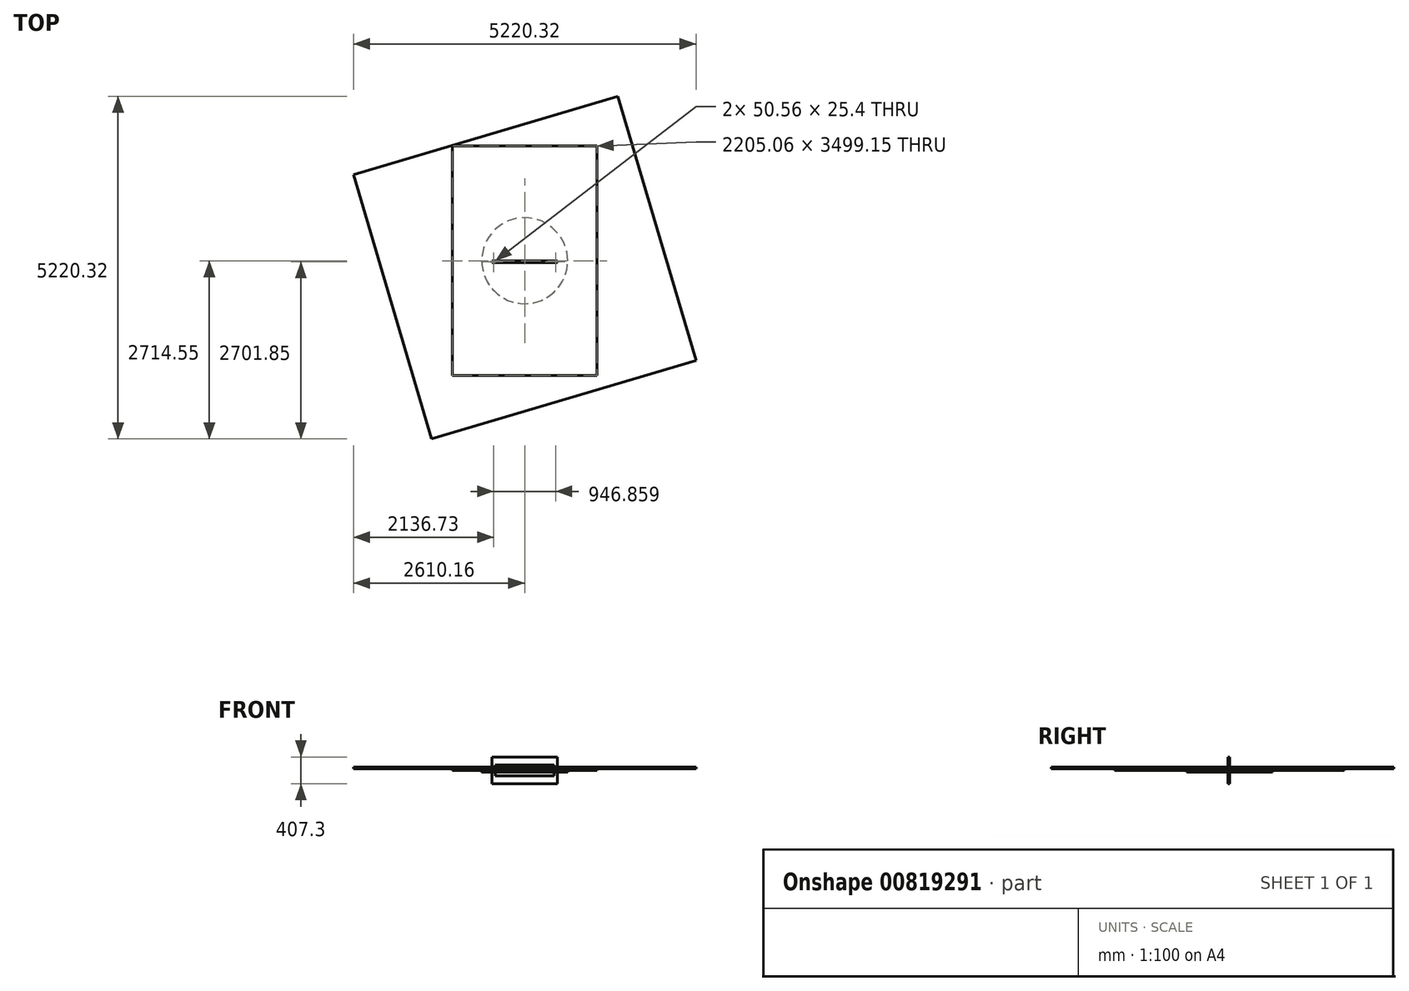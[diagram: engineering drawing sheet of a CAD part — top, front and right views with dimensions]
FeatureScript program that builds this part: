
annotation { "Feature Type Name" : "Feature", "Feature Type Description" : "" }
export const myFeature = defineFeature(function(context is Context, id is Id, definition is map)
    precondition{}
    {
        {
            var Q0;
            Q0=qCreatedBy(makeId("Front.planeOp"),FACE);
            var sketch = newSketch(context, id + "F0", { "sketchPlane" : qUnion([Q0])});
            skLineSegment(sketch, "E0.bottom", {"start": v(448.15, -82.7) * mm, "end": v(-448.15, -82.7) * mm});
            skLineSegment(sketch, "E0.top", {"start": v(448.15, 82.7) * mm, "end": v(-448.15, 82.7) * mm});
            skLineSegment(sketch, "E0.left", {"start": v(448.15, -82.7) * mm, "end": v(448.15, 82.7) * mm});
            skLineSegment(sketch, "E0.right", {"start": v(-448.15, -82.7) * mm, "end": v(-448.15, 82.7) * mm});
            skPoint(sketch, "E0.middle", {"position": v(0, 0) * mm});
            skLineSegment(sketch, "E1.bottom", {"start": v(-498.7, 203.65) * mm, "end": v(498.7, 203.65) * mm});
            skLineSegment(sketch, "E1.top", {"start": v(-498.7, -203.65) * mm, "end": v(498.7, -203.65) * mm});
            skLineSegment(sketch, "E1.left", {"start": v(-498.7, 203.65) * mm, "end": v(-498.7, -203.65) * mm});
            skLineSegment(sketch, "E1.right", {"start": v(498.7, 203.65) * mm, "end": v(498.7, -203.65) * mm});
            skSolve(sketch);
        }
        {
            var Q0;
            Q0=makeQuery(id+"F0.imprint","IMPRINT",FACE,{"disambiguationData":[TD([[makeQuery(id+"F0.imprint","IMPRINT",EDGE,{"derivedFrom":sQuery(id+"F0.wireOp",EDGE,"E0.bottom")}),1.0]])]});
            extrude(context, id + "F1", {"entities" : qUnion([Q0]), "depth" : 25.4 * mm, "offsetDistance" : 25.4 * mm});
        }
        {
            var Q0;
            Q0=qCreatedBy(makeId("Top.planeOp"),FACE);
            var sketch = newSketch(context, id + "F2", { "sketchPlane" : qUnion([Q0])});
            skLineSegment(sketch, "E2.bottom", {"start": v(-1102.53, -1749.57) * mm, "end": v(1102.53, -1749.57) * mm});
            skLineSegment(sketch, "E2.top", {"start": v(-1102.53, 1749.57) * mm, "end": v(1102.53, 1749.57) * mm});
            skLineSegment(sketch, "E2.left", {"start": v(-1102.53, -1749.57) * mm, "end": v(-1102.53, 1749.57) * mm});
            skLineSegment(sketch, "E2.right", {"start": v(1102.53, -1749.57) * mm, "end": v(1102.53, 1749.57) * mm});
            skPoint(sketch, "E2.middle", {"position": v(0, 0) * mm});
            skSolve(sketch);
        }
        {
            var Q0;
            Q0=makeQuery(id+"F2.imprint","IMPRINT",FACE,{"disambiguationData":[TD([[makeQuery(id+"F2.imprint","IMPRINT",EDGE,{"derivedFrom":sQuery(id+"F2.wireOp",EDGE,"E2.bottom")}),1.0]])]});
            extrude(context, id + "F3", {"entities" : qUnion([Q0]), "operationType" : NewBodyOperationType.ADD, "depth" : 25.4 * mm, "offsetDistance" : 25.4 * mm});
        }
        {
            var Q0;
            Q0=makeQuery(id+"F3.opExtrude","CAP_FACE",FACE,{"disambiguationData":[OSD([sQuery(id+"F2.wireOp",EDGE,"E2.bottom"),sQuery(id+"F2.wireOp",EDGE,"E2.top"),sQuery(id+"F2.wireOp",EDGE,"E2.left"),sQuery(id+"F2.wireOp",EDGE,"E2.right")])],"isStart":true});
            var sketch = newSketch(context, id + "F4", { "sketchPlane" : qUnion([Q0])});
            skCircle(sketch, "E3", {"center": v(0, 0) * mm, "radius": 654.69 * mm});
            skCircle(sketch, "E4", {"center": v(0, 0) * mm, "radius": 953.45 * mm});
            skCircle(sketch, "E5", {"center": v(0, 0) * mm, "radius": 1245.2 * mm});
            skSolve(sketch);
        }
        {
            var Q0;
            Q0=makeQuery(id+"F4.imprint","IMPRINT",FACE,{"disambiguationData":[TD([[makeQuery(id+"F4.imprint","IMPRINT",EDGE,{"derivedFrom":sQuery(id+"F4.wireOp",EDGE,"E3")}),1.0]])]});
            extrude(context, id + "F5", {"entities" : qUnion([Q0]), "operationType" : NewBodyOperationType.ADD, "depth" : 25.4 * mm, "offsetDistance" : 25.4 * mm});
        }
        {
            var Q0;
            Q0=makeQuery(id+"F3.opExtrude","CAP_FACE",FACE,{"disambiguationData":[OSD([sQuery(id+"F2.wireOp",EDGE,"E2.bottom"),sQuery(id+"F2.wireOp",EDGE,"E2.top"),sQuery(id+"F2.wireOp",EDGE,"E2.left"),sQuery(id+"F2.wireOp",EDGE,"E2.right")])],"isStart":false});
            var sketch = newSketch(context, id + "F6", { "sketchPlane" : qUnion([Q0])});
            skSolve(sketch);
        }
        {
            var Q0;
            {var subQ3=sQuery(id+"F2.wireOp",EDGE,"E2.bottom");Q0=makeQuery(id+"F6.imprint","IMPRINT",FACE,{"disambiguationData":[TD([[makeQuery(id+"F6.imprint","IMPRINT",EDGE,{"derivedFrom":makeQuery(id+"F3.opExtrude","CAP_EDGE",EDGE,{"disambiguationData":[OSD([subQ3])],"isStart":false})}),1.0]])]});}
            var sketch = newSketch(context, id + "F7", { "sketchPlane" : qUnion([Q0])});
            skCircle(sketch, "E6.cCircle", {"center": v(0, -104.4) * mm, "radius": 2100.34 * mm, "construction": true});
            skLineSegment(sketch, "E6.0", {"start": v(-2610.16, 1313.33) * mm, "end": v(1417.73, 2505.77) * mm});
            skLineSegment(sketch, "E6.1", {"start": v(1417.73, 2505.77) * mm, "end": v(2610.16, -1522.12) * mm});
            skLineSegment(sketch, "E6.2", {"start": v(2610.16, -1522.12) * mm, "end": v(-1417.73, -2714.55) * mm});
            skLineSegment(sketch, "E6.3", {"start": v(-1417.73, -2714.55) * mm, "end": v(-2610.16, 1313.33) * mm});
            skPoint(sketch, "E6.0.midPoint", {"position": v(-596.22, 1909.55) * mm});
            skSolve(sketch);
        }
        {
            var Q0;
            Q0=makeQuery(id+"F7.imprint","IMPRINT",FACE,{"disambiguationData":[TD([[makeQuery(id+"F7.imprint","IMPRINT",EDGE,{"derivedFrom":sQuery(id+"F7.wireOp",EDGE,"E6.0")}),-1.0]])]});
            var sketch = newSketch(context, id + "F8", { "sketchPlane" : qUnion([Q0])});
            skSolve(sketch);
        }
        {
            var Q0;
            Q0=makeQuery(id+"F8.imprint","IMPRINT",FACE,{"disambiguationData":[TD([[makeQuery(id+"F8.imprint","IMPRINT",EDGE,{"derivedFrom":makeQuery(id+"F7.imprint","IMPRINT",EDGE,{"derivedFrom":sQuery(id+"F7.wireOp",EDGE,"E6.0")})}),-1.0]])]});
            extrude(context, id + "F9", {"entities" : qUnion([Q0]), "depth" : 25.4 * mm, "offsetDistance" : 25.4 * mm});
        }
    });
